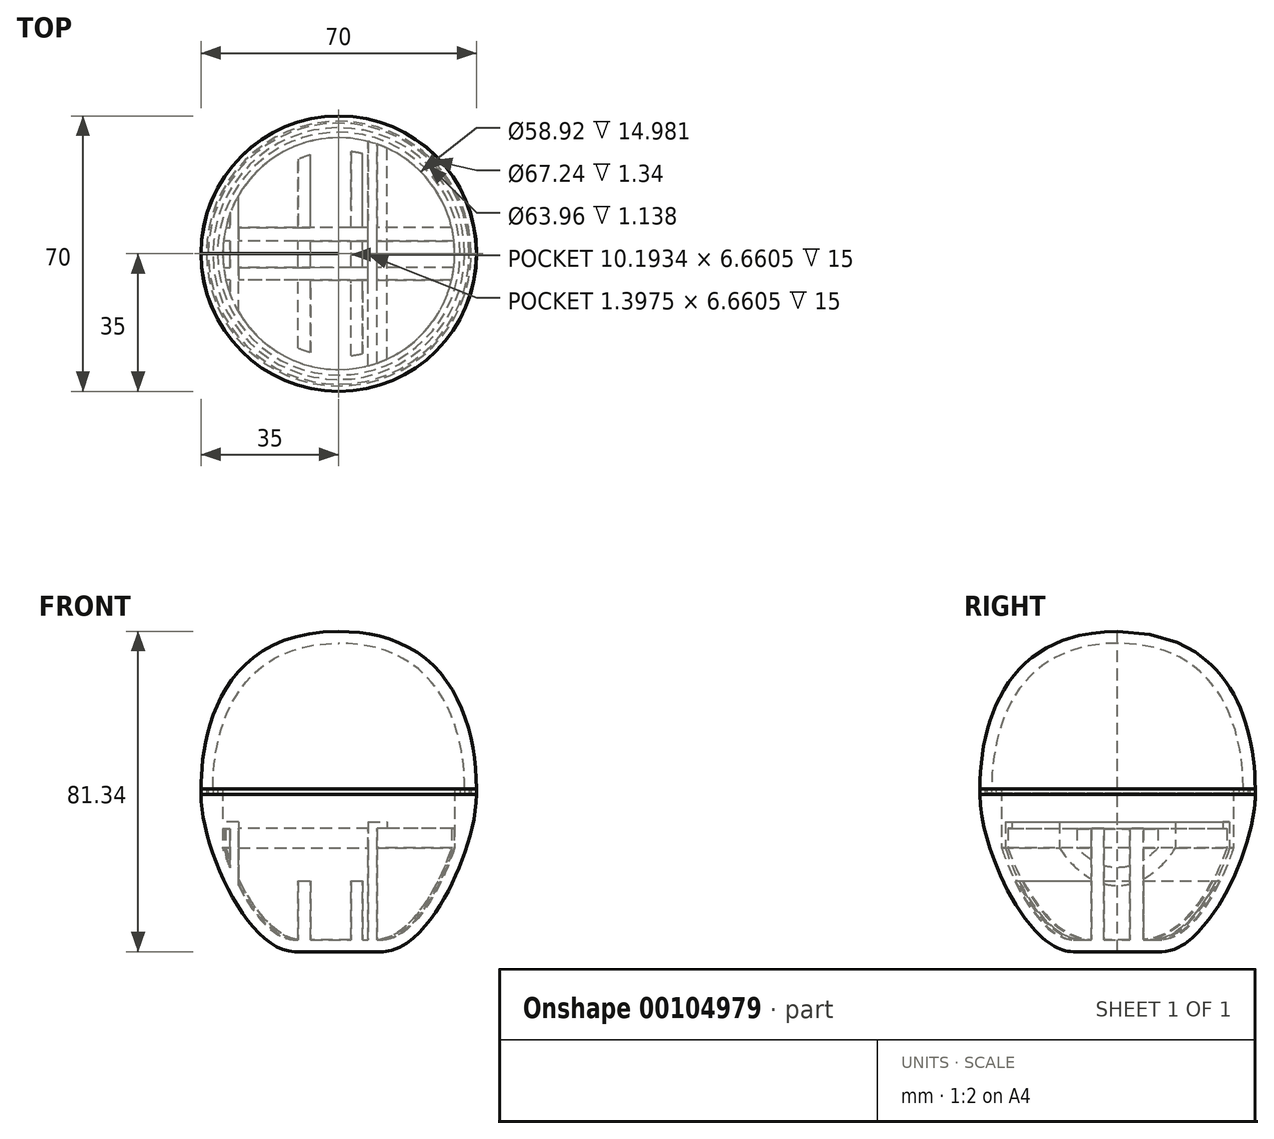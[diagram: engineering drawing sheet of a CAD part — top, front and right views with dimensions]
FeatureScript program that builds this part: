
annotation { "Feature Type Name" : "Feature", "Feature Type Description" : "" }
export const myFeature = defineFeature(function(context is Context, id is Id, definition is map)
    precondition{}
    {
        {
            var Q0;
            Q0=qCreatedBy(makeId("Front.planeOp"),FACE);
            var sketch = newSketch(context, id + "F0", { "sketchPlane" : qUnion([Q0])});
            skLineSegment(sketch, "E0", {"start": v(0, 0) * mm, "end": v(11.25, 0) * mm});
            skFitSpline(sketch, "E1", {"points": [v(11.25, 0) * mm, v(35, 40) * mm], "startDerivative": vector(35.37, 0) * mm, "endDerivative": vector(0, 40.87) * mm});
            skFitSpline(sketch, "E2", {"points": [v(32, 40) * mm, v(11.25, 3) * mm], "startDerivative": vector(0, -39.3) * mm, "endDerivative": vector(-30.2, 0) * mm});
            skLineSegment(sketch, "E3", {"start": v(11.25, -3.76) * mm, "end": v(11.25, 7.66) * mm, "construction": true});
            skLineSegment(sketch, "E4", {"start": v(41.27, 40) * mm, "end": v(22.73, 40) * mm, "construction": true});
            skLineSegment(sketch, "E5", {"start": v(35, 40) * mm, "end": v(32, 40) * mm});
            skLineSegment(sketch, "E6", {"start": v(11.25, 3) * mm, "end": v(0, 3) * mm});
            skLineSegment(sketch, "E7", {"start": v(0, 3) * mm, "end": v(0, 0) * mm});
            skLineSegment(sketch, "E8", {"start": v(32, 40) * mm, "end": v(29.46, 40) * mm});
            skLineSegment(sketch, "E9", {"start": v(29.46, 40) * mm, "end": v(29.46, 26.36) * mm});
            skLineSegment(sketch, "E10", {"start": v(29.46, 40) * mm, "end": v(29.46, 41.34) * mm});
            skLineSegment(sketch, "E11", {"start": v(29.46, 41.34) * mm, "end": v(30.83, 41.34) * mm});
            skLineSegment(sketch, "E12", {"start": v(30.83, 41.34) * mm, "end": v(30.83, 40) * mm});
            skLineSegment(sketch, "E13", {"start": v(35, 40) * mm, "end": v(35, 41.34) * mm});
            skLineSegment(sketch, "E14", {"start": v(35, 41.34) * mm, "end": v(33.62, 41.34) * mm});
            skLineSegment(sketch, "E15", {"start": v(33.62, 41.34) * mm, "end": v(33.62, 40) * mm});
            skSolve(sketch);
        }
        {
            var Q0;
            Q0=qCreatedBy(makeId("Front.planeOp"),FACE);
            var sketch = newSketch(context, id + "F1", { "sketchPlane" : qUnion([Q0])});
            skLineSegment(sketch, "E16", {"start": v(0, -39.7) * mm, "end": v(0, 92.25) * mm, "construction": true});
            skSolve(sketch);
        }
        {
            var Q0;
            Q0 = qSketchRegion(id + "F0", true);
            var Q1;
            Q1=sQuery(id+"F1.wireOp",EDGE,"E16");
            revolve(context, id + "F2", {"entities" : qUnion([Q0]), "axis" : qUnion([Q1]), "revolveType" : RevolveType.FULL});
        }
        {
            var Q0;
            Q0=qCreatedBy(makeId("Front.planeOp"),FACE);
            var sketch = newSketch(context, id + "F3", { "sketchPlane" : qUnion([Q0])});
            skLineSegment(sketch, "E17", {"start": v(-25.5, 33) * mm, "end": v(-29.7, 33) * mm});
            skLineSegment(sketch, "E18", {"start": v(-29.7, 33) * mm, "end": v(-29.7, 31.22) * mm});
            skLineSegment(sketch, "E19", {"start": v(-29.7, 31.22) * mm, "end": v(-25.5, 31.22) * mm});
            skLineSegment(sketch, "E20", {"start": v(-25.5, 31.22) * mm, "end": v(-25.5, 33) * mm});
            skLineSegment(sketch, "E21", {"start": v(-10.27, 18) * mm, "end": v(-7.13, 18) * mm});
            skLineSegment(sketch, "E22", {"start": v(-7.13, 18) * mm, "end": v(-7.13, 3) * mm});
            skLineSegment(sketch, "E23", {"start": v(-7.13, 3) * mm, "end": v(-10.27, 3) * mm});
            skLineSegment(sketch, "E24", {"start": v(-10.27, 3) * mm, "end": v(-10.27, 18) * mm});
            skLineSegment(sketch, "E25", {"start": v(3.06, 18) * mm, "end": v(6.1, 18) * mm});
            skLineSegment(sketch, "E26", {"start": v(6.1, 18) * mm, "end": v(6.1, 3) * mm});
            skLineSegment(sketch, "E27", {"start": v(6.1, 3) * mm, "end": v(3.06, 3) * mm});
            skLineSegment(sketch, "E28", {"start": v(3.06, 3) * mm, "end": v(3.06, 18) * mm});
            skLineSegment(sketch, "E29", {"start": v(7.5, 33) * mm, "end": v(12.27, 33) * mm});
            skLineSegment(sketch, "E30", {"start": v(12.27, 33) * mm, "end": v(12.27, 31.3) * mm});
            skLineSegment(sketch, "E31", {"start": v(12.27, 31.3) * mm, "end": v(7.5, 31.3) * mm});
            skLineSegment(sketch, "E32", {"start": v(7.5, 31.3) * mm, "end": v(7.5, 33) * mm});
            skLineSegment(sketch, "E33", {"start": v(-27.6, 31.22) * mm, "end": v(-27.6, 16.36) * mm});
            skLineSegment(sketch, "E34", {"start": v(-27.6, 16.36) * mm, "end": v(-25.5, 16.36) * mm});
            skLineSegment(sketch, "E35", {"start": v(-25.5, 16.36) * mm, "end": v(-25.5, 31.22) * mm});
            skLineSegment(sketch, "E36", {"start": v(7.5, 31.3) * mm, "end": v(7.5, 2.68) * mm});
            skLineSegment(sketch, "E37", {"start": v(7.5, 2.68) * mm, "end": v(9.67, 2.68) * mm});
            skLineSegment(sketch, "E38", {"start": v(9.67, 2.68) * mm, "end": v(9.67, 31.3) * mm});
            skSolve(sketch);
        }
        {
            var Q0;
            Q0=qCreatedBy(makeId("Front.planeOp"),FACE);
            var sketch = newSketch(context, id + "F4", { "sketchPlane" : qUnion([Q0])});
            skLineSegment(sketch, "E39", {"start": v(-25.5, 18) * mm, "end": v(7.5, 18) * mm});
            skLineSegment(sketch, "E40", {"start": v(7.5, 18) * mm, "end": v(7.5, 40) * mm});
            skLineSegment(sketch, "E41", {"start": v(7.5, 40) * mm, "end": v(-25.5, 40) * mm});
            skLineSegment(sketch, "E42", {"start": v(-25.5, 40) * mm, "end": v(-25.5, 18) * mm});
            skLineSegment(sketch, "E43", {"start": v(7.5, 40) * mm, "end": v(7.5, 48) * mm});
            skLineSegment(sketch, "E44", {"start": v(7.5, 48) * mm, "end": v(-7.5, 48) * mm});
            skLineSegment(sketch, "E45", {"start": v(-7.5, 48) * mm, "end": v(-7.5, 40) * mm});
            skPoint(sketch, "E46", {"position": v(0, 48) * mm});
            skLineSegment(sketch, "E47", {"start": v(-25.5, 33) * mm, "end": v(-27.96, 33) * mm});
            skLineSegment(sketch, "E48", {"start": v(-27.96, 33) * mm, "end": v(-27.96, 35.1) * mm});
            skLineSegment(sketch, "E49", {"start": v(-27.96, 35.1) * mm, "end": v(-25.5, 35.1) * mm});
            skLineSegment(sketch, "E50", {"start": v(7.5, 33) * mm, "end": v(10.19, 33) * mm});
            skLineSegment(sketch, "E51", {"start": v(10.19, 33) * mm, "end": v(10.19, 35.1) * mm});
            skLineSegment(sketch, "E52", {"start": v(10.19, 35.1) * mm, "end": v(7.5, 35.1) * mm});
            skSolve(sketch);
        }
        {
            var Q0;
            Q0 = qSketchRegion(id + "F3", true);
            extrude(context, id + "F5", {"entities" : qUnion([Q0]), "operationType" : NewBodyOperationType.ADD, "endBound" : BoundingType.UP_TO_NEXT, "depth" : 25 * mm});
        }
        {
            var Q0;
            Q0 = qSketchRegion(id + "F3", true);
            extrude(context, id + "F6", {"entities" : qUnion([Q0]), "operationType" : NewBodyOperationType.ADD, "endBound" : BoundingType.UP_TO_NEXT, "oppositeDirection" : true, "depth" : 25 * mm});
        }
        {
            var Q0;
            Q0=qCreatedBy(makeId("Right.planeOp"),FACE);
            var sketch = newSketch(context, id + "F7", { "sketchPlane" : qUnion([Q0])});
            skLineSegment(sketch, "E53", {"start": v(-3.51, 31.26) * mm, "end": v(-3.51, 1.9) * mm});
            skLineSegment(sketch, "E54", {"start": v(-3.51, 1.9) * mm, "end": v(-6.68, 1.9) * mm});
            skLineSegment(sketch, "E55", {"start": v(-6.68, 1.9) * mm, "end": v(-6.68, 31.26) * mm});
            skLineSegment(sketch, "E56", {"start": v(-6.68, 31.26) * mm, "end": v(-3.51, 31.26) * mm});
            skLineSegment(sketch, "E57", {"start": v(3.15, 31.26) * mm, "end": v(6.6, 31.26) * mm});
            skLineSegment(sketch, "E58", {"start": v(6.6, 31.26) * mm, "end": v(6.6, 1.9) * mm});
            skLineSegment(sketch, "E59", {"start": v(6.6, 1.9) * mm, "end": v(3.15, 1.9) * mm});
            skLineSegment(sketch, "E60", {"start": v(3.15, 1.9) * mm, "end": v(3.15, 31.26) * mm});
            skSolve(sketch);
        }
        {
            var Q0;
            Q0 = qSketchRegion(id + "F7", true);
            var Q1;
            Q1=makeQuery(id+"F2.opRevolve","SWEPT_BODY",BODY,{"disambiguationData":[OSD([sQuery(id+"F0.wireOp",EDGE,"E0"),sQuery(id+"F0.wireOp",EDGE,"E1"),sQuery(id+"F0.wireOp",EDGE,"E2"),sQuery(id+"F0.wireOp",EDGE,"E5"),sQuery(id+"F0.wireOp",EDGE,"E6"),sQuery(id+"F0.wireOp",EDGE,"E7"),sQuery(id+"F0.wireOp",EDGE,"E8"),sQuery(id+"F0.wireOp",EDGE,"E9"),sQuery(id+"F0.wireOp",EDGE,"E10"),sQuery(id+"F0.wireOp",EDGE,"E11"),sQuery(id+"F0.wireOp",EDGE,"E12"),sQuery(id+"F0.wireOp",EDGE,"E13"),sQuery(id+"F0.wireOp",EDGE,"E14"),sQuery(id+"F0.wireOp",EDGE,"E15")])]});
            extrude(context, id + "F8", {"entities" : qUnion([Q0]), "operationType" : NewBodyOperationType.ADD, "endBound" : BoundingType.UP_TO_BODY, "endBoundEntityBody" : qUnion([Q1]), "depth" : 25 * mm});
        }
        {
            var Q0;
            Q0 = qSketchRegion(id + "F7", true);
            var Q1;
            Q1=makeQuery(id+"F2.opRevolve","SWEPT_BODY",BODY,{"disambiguationData":[OSD([sQuery(id+"F0.wireOp",EDGE,"E0"),sQuery(id+"F0.wireOp",EDGE,"E1"),sQuery(id+"F0.wireOp",EDGE,"E2"),sQuery(id+"F0.wireOp",EDGE,"E5"),sQuery(id+"F0.wireOp",EDGE,"E6"),sQuery(id+"F0.wireOp",EDGE,"E7"),sQuery(id+"F0.wireOp",EDGE,"E8"),sQuery(id+"F0.wireOp",EDGE,"E9"),sQuery(id+"F0.wireOp",EDGE,"E10"),sQuery(id+"F0.wireOp",EDGE,"E11"),sQuery(id+"F0.wireOp",EDGE,"E12"),sQuery(id+"F0.wireOp",EDGE,"E13"),sQuery(id+"F0.wireOp",EDGE,"E14"),sQuery(id+"F0.wireOp",EDGE,"E15")])]});
            extrude(context, id + "F9", {"entities" : qUnion([Q0]), "operationType" : NewBodyOperationType.ADD, "endBound" : BoundingType.UP_TO_BODY, "oppositeDirection" : true, "endBoundEntityBody" : qUnion([Q1]), "depth" : 25 * mm});
        }
        {
            var Q0;
            Q0=qCreatedBy(makeId("Front.planeOp"),FACE);
            var sketch = newSketch(context, id + "F10", { "sketchPlane" : qUnion([Q0])});
            skFitSpline(sketch, "E61", {"points": [v(-34.98, 41.34) * mm, v(0, 81.34) * mm], "startDerivative": vector(0, 35.63) * mm, "endDerivative": vector(94.24, 0) * mm});
            skLineSegment(sketch, "E62", {"start": v(-34.98, 53.22) * mm, "end": v(-34.98, 34.92) * mm, "construction": true});
            skLineSegment(sketch, "E63", {"start": v(0, 81.34) * mm, "end": v(0, 78.34) * mm});
            skLineSegment(sketch, "E64", {"start": v(-34.98, 41.34) * mm, "end": v(-31.98, 41.34) * mm});
            skFitSpline(sketch, "E65", {"points": [v(-31.98, 41.34) * mm, v(0, 78.34) * mm], "startDerivative": vector(0, 47.01) * mm, "endDerivative": vector(77.1, 0) * mm});
            skLineSegment(sketch, "E66", {"start": v(-33.15, 41.34) * mm, "end": v(-33.15, 40.2) * mm});
            skLineSegment(sketch, "E67", {"start": v(-33.15, 40.2) * mm, "end": v(-31.98, 40.2) * mm});
            skLineSegment(sketch, "E68", {"start": v(-31.98, 40.2) * mm, "end": v(-31.98, 41.34) * mm});
            skSolve(sketch);
        }
        {
            var Q0;
            Q0 = qSketchRegion(id + "F10", true);
            var Q1;
            Q1=sQuery(id+"F1.wireOp",EDGE,"E16");
            revolve(context, id + "F11", {"entities" : qUnion([Q0]), "axis" : qUnion([Q1]), "revolveType" : RevolveType.FULL});
        }
    });
